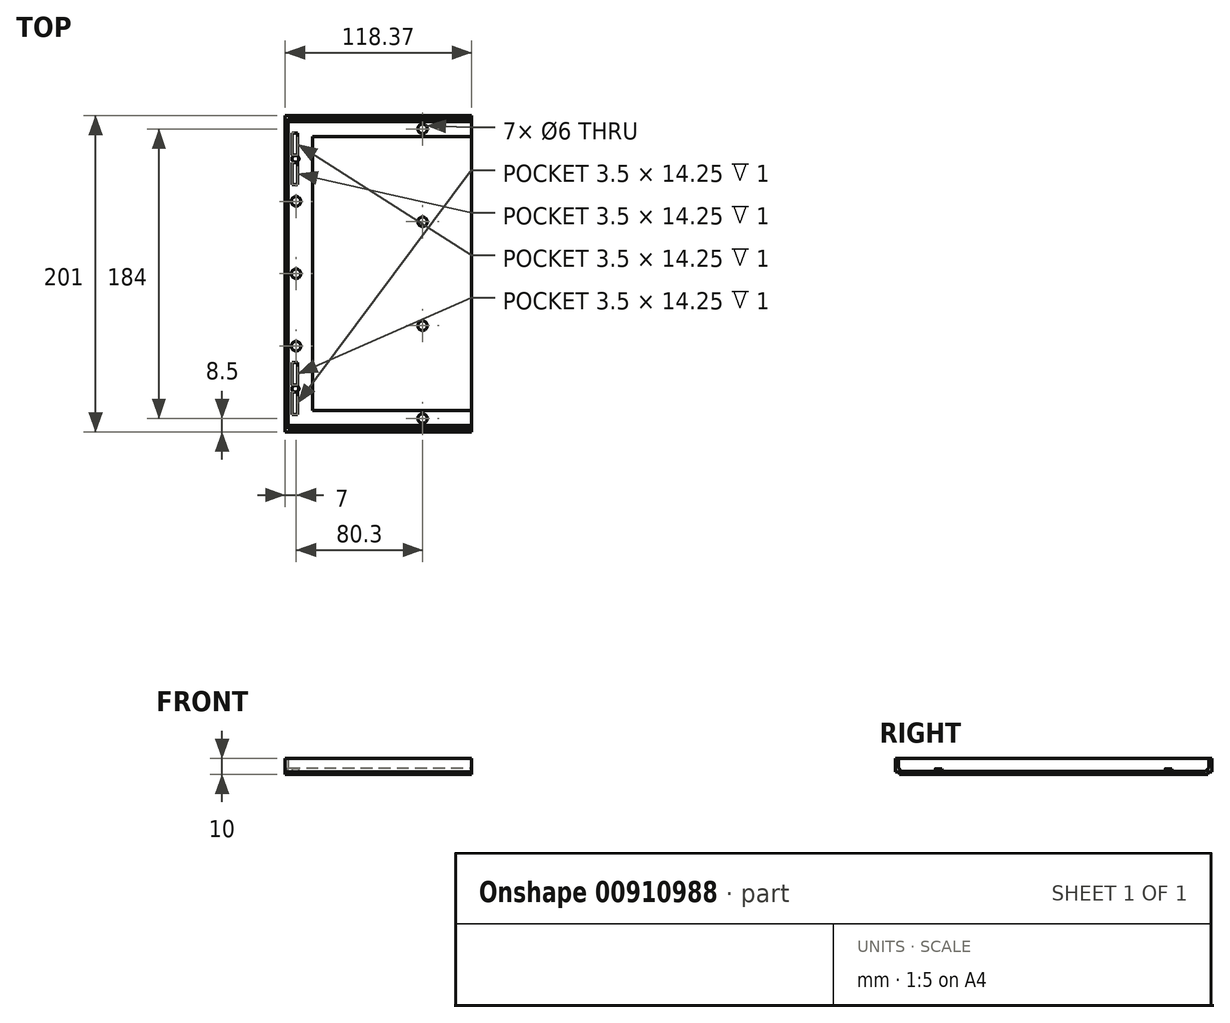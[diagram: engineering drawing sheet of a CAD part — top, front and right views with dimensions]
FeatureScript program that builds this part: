
annotation { "Feature Type Name" : "Feature", "Feature Type Description" : "" }
export const myFeature = defineFeature(function(context is Context, id is Id, definition is map)
    precondition{}
    {
        {
            var Q0;
            Q0=qCreatedBy(makeId("Top.planeOp"),FACE);
            var sketch = newSketch(context, id + "F0", { "sketchPlane" : qUnion([Q0])});
            skLineSegment(sketch, "E0.bottom", {"start": v(0, 0) * mm, "end": v(245, 0) * mm});
            skLineSegment(sketch, "E0.top", {"start": v(0, -201) * mm, "end": v(245, -201) * mm});
            skLineSegment(sketch, "E0.left", {"start": v(0, 0) * mm, "end": v(0, -201) * mm});
            skLineSegment(sketch, "E0.right", {"start": v(245, 0) * mm, "end": v(245, -201) * mm});
            skSolve(sketch);
        }
        {
            var Q0;
            Q0=qSketchRegion(id+"F0",true);
            extrude(context, id + "F1", {"entities" : qUnion([Q0]), "depth" : 8 * mm, "offsetDistance" : 25 * mm});
        }
        {
            var Q0;
            Q0=makeQuery(id+"F1.opExtrude","CAP_FACE",FACE,{"disambiguationData":[OSD([sQuery(id+"F0.wireOp",EDGE,"E0.bottom"),sQuery(id+"F0.wireOp",EDGE,"E0.top"),sQuery(id+"F0.wireOp",EDGE,"E0.left"),sQuery(id+"F0.wireOp",EDGE,"E0.right")])],"isStart":false});
            shell(context, id + "F2", {"entities" : qUnion([Q0]), "thickness" : 2 * mm});
        }
        {
            var Q0;
            Q0=makeQuery(id+"F2.opShell","OFFSET_FACE",FACE,{"disambiguationData":[OSD([sQuery(id+"F0.wireOp",EDGE,"E0.bottom"),sQuery(id+"F0.wireOp",EDGE,"E0.top"),sQuery(id+"F0.wireOp",EDGE,"E0.left"),sQuery(id+"F0.wireOp",EDGE,"E0.right")])]});
            var sketch = newSketch(context, id + "F3", { "sketchPlane" : qUnion([Q0])});
            skLineSegment(sketch, "E1.bottom", {"start": v(17.5, -13.5) * mm, "end": v(227.5, -13.5) * mm});
            skLineSegment(sketch, "E1.top", {"start": v(17.5, -187.5) * mm, "end": v(227.5, -187.5) * mm});
            skLineSegment(sketch, "E1.left", {"start": v(17.5, -13.5) * mm, "end": v(17.5, -187.5) * mm});
            skLineSegment(sketch, "E1.right", {"start": v(227.5, -13.5) * mm, "end": v(227.5, -187.5) * mm});
            skSolve(sketch);
        }
        {
            var Q0;
            Q0=qSketchRegion(id+"F3",true);
            extrude(context, id + "F4", {"entities" : qUnion([Q0]), "operationType" : NewBodyOperationType.REMOVE, "oppositeDirection" : true, "depth" : 1 * mm, "offsetDistance" : 25 * mm});
        }
        {
            var Q0;
            Q0=makeQuery(id+"F2.opShell","OFFSET_FACE",FACE,{"disambiguationData":[OSD([sQuery(id+"F0.wireOp",EDGE,"E0.bottom"),sQuery(id+"F0.wireOp",EDGE,"E0.top"),sQuery(id+"F0.wireOp",EDGE,"E0.left"),sQuery(id+"F0.wireOp",EDGE,"E0.right")])]});
            var sketch = newSketch(context, id + "F5", { "sketchPlane" : qUnion([Q0])});
            skLineSegment(sketch, "E2.bottom", {"start": v(4.5, -11) * mm, "end": v(8, -11) * mm});
            skLineSegment(sketch, "E2.top", {"start": v(4.5, -44) * mm, "end": v(8, -44) * mm});
            skLineSegment(sketch, "E2.left", {"start": v(4.5, -11) * mm, "end": v(4.5, -44) * mm});
            skLineSegment(sketch, "E2.right", {"start": v(8, -11) * mm, "end": v(8, -44) * mm});
            skLineSegment(sketch, "E3.bottom", {"start": v(4.5, -157) * mm, "end": v(8, -157) * mm});
            skLineSegment(sketch, "E3.top", {"start": v(4.5, -190) * mm, "end": v(8, -190) * mm});
            skLineSegment(sketch, "E3.left", {"start": v(4.5, -157) * mm, "end": v(4.5, -190) * mm});
            skLineSegment(sketch, "E3.right", {"start": v(8, -157) * mm, "end": v(8, -190) * mm});
            skLineSegment(sketch, "E4.bottom", {"start": v(237, -11) * mm, "end": v(240.5, -11) * mm});
            skLineSegment(sketch, "E4.top", {"start": v(237, -44) * mm, "end": v(240.5, -44) * mm});
            skLineSegment(sketch, "E4.left", {"start": v(237, -11) * mm, "end": v(237, -44) * mm});
            skLineSegment(sketch, "E4.right", {"start": v(240.5, -11) * mm, "end": v(240.5, -44) * mm});
            skLineSegment(sketch, "E5.bottom", {"start": v(237, -157) * mm, "end": v(240.5, -157) * mm});
            skLineSegment(sketch, "E5.top", {"start": v(237, -190) * mm, "end": v(240.5, -190) * mm});
            skLineSegment(sketch, "E5.left", {"start": v(237, -157) * mm, "end": v(237, -190) * mm});
            skLineSegment(sketch, "E5.right", {"start": v(240.5, -157) * mm, "end": v(240.5, -190) * mm});
            skSolve(sketch);
        }
        {
            var Q0;
            Q0=qSketchRegion(id+"F5",true);
            extrude(context, id + "F6", {"entities" : qUnion([Q0]), "operationType" : NewBodyOperationType.REMOVE, "oppositeDirection" : true, "depth" : 1 * mm, "offsetDistance" : 25 * mm});
        }
        {
            var Q0;
            Q0=makeQuery(id+"F2.opShell","OFFSET_FACE",FACE,{"disambiguationData":[OSD([sQuery(id+"F0.wireOp",EDGE,"E0.bottom"),sQuery(id+"F0.wireOp",EDGE,"E0.top"),sQuery(id+"F0.wireOp",EDGE,"E0.left"),sQuery(id+"F0.wireOp",EDGE,"E0.right")])]});
            var sketch = newSketch(context, id + "F7", { "sketchPlane" : qUnion([Q0])});
            skCircle(sketch, "E6", {"center": v(238, -7) * mm, "radius": 2.75 * mm});
            skCircle(sketch, "E7", {"center": v(7, -7) * mm, "radius": 2.75 * mm});
            skCircle(sketch, "E8", {"center": v(7, -194) * mm, "radius": 2.75 * mm});
            skCircle(sketch, "E9", {"center": v(238, -194) * mm, "radius": 2.75 * mm});
            skSolve(sketch);
        }
        {
            var Q0;
            Q0=makeQuery(id+"F2.opShell","OFFSET_FACE",FACE,{"disambiguationData":[OSD([sQuery(id+"F0.wireOp",EDGE,"E0.bottom"),sQuery(id+"F0.wireOp",EDGE,"E0.top"),sQuery(id+"F0.wireOp",EDGE,"E0.left"),sQuery(id+"F0.wireOp",EDGE,"E0.right")])]});
            var sketch = newSketch(context, id + "F8", { "sketchPlane" : qUnion([Q0])});
            skLineSegment(sketch, "E10", {"start": v(237, -175.75) * mm, "end": v(240.5, -175.75) * mm});
            skLineSegment(sketch, "E11", {"start": v(240.5, -175.75) * mm, "end": v(240.5, -171.25) * mm});
            skLineSegment(sketch, "E12", {"start": v(240.5, -171.25) * mm, "end": v(237, -171.25) * mm});
            skLineSegment(sketch, "E13", {"start": v(237, -175.75) * mm, "end": v(237, -171.25) * mm});
            skLineSegment(sketch, "E14.bottom", {"start": v(240.5, -25.25) * mm, "end": v(237, -25.25) * mm});
            skLineSegment(sketch, "E14.top", {"start": v(240.5, -29.75) * mm, "end": v(237, -29.75) * mm});
            skLineSegment(sketch, "E14.left", {"start": v(240.5, -25.25) * mm, "end": v(240.5, -29.75) * mm});
            skLineSegment(sketch, "E14.right", {"start": v(237, -25.25) * mm, "end": v(237, -29.75) * mm});
            skLineSegment(sketch, "E15.bottom", {"start": v(8, -25.25) * mm, "end": v(4.5, -25.25) * mm});
            skLineSegment(sketch, "E15.top", {"start": v(8, -29.75) * mm, "end": v(4.5, -29.75) * mm});
            skLineSegment(sketch, "E15.left", {"start": v(8, -25.25) * mm, "end": v(8, -29.75) * mm});
            skLineSegment(sketch, "E15.right", {"start": v(4.5, -25.25) * mm, "end": v(4.5, -29.75) * mm});
            skLineSegment(sketch, "E16.bottom", {"start": v(8, -175.75) * mm, "end": v(4.5, -175.75) * mm});
            skLineSegment(sketch, "E16.top", {"start": v(8, -171.25) * mm, "end": v(4.5, -171.25) * mm});
            skLineSegment(sketch, "E16.left", {"start": v(8, -175.75) * mm, "end": v(8, -171.25) * mm});
            skLineSegment(sketch, "E16.right", {"start": v(4.5, -175.75) * mm, "end": v(4.5, -171.25) * mm});
            skSolve(sketch);
        }
        {
            var Q0;
            Q0=qSketchRegion(id+"F8",true);
            extrude(context, id + "F9", {"entities" : qUnion([Q0]), "operationType" : NewBodyOperationType.ADD, "oppositeDirection" : true, "depth" : 1 * mm, "offsetDistance" : 25 * mm});
        }
        {
            var Q0;
            Q0=makeQuery(id+"F9.boolean.opBoolean","MERGE",FACE,{"derivedFrom":[makeQuery(id+"F2.opShell","OFFSET_FACE",FACE,{"disambiguationData":[OSD([sQuery(id+"F0.wireOp",EDGE,"E0.bottom"),sQuery(id+"F0.wireOp",EDGE,"E0.top"),sQuery(id+"F0.wireOp",EDGE,"E0.left"),sQuery(id+"F0.wireOp",EDGE,"E0.right")])]}),makeQuery(id+"F9.opExtrude","CAP_FACE",FACE,{"disambiguationData":[OSD([sQuery(id+"F8.wireOp",EDGE,"E10"),sQuery(id+"F8.wireOp",EDGE,"E11"),sQuery(id+"F8.wireOp",EDGE,"E12"),sQuery(id+"F8.wireOp",EDGE,"E13")])],"isStart":true}),makeQuery(id+"F9.opExtrude","CAP_FACE",FACE,{"disambiguationData":[OSD([sQuery(id+"F8.wireOp",EDGE,"E14.bottom"),sQuery(id+"F8.wireOp",EDGE,"E14.top"),sQuery(id+"F8.wireOp",EDGE,"E14.left"),sQuery(id+"F8.wireOp",EDGE,"E14.right")])],"isStart":true}),makeQuery(id+"F9.opExtrude","CAP_FACE",FACE,{"disambiguationData":[OSD([sQuery(id+"F8.wireOp",EDGE,"E15.bottom"),sQuery(id+"F8.wireOp",EDGE,"E15.top"),sQuery(id+"F8.wireOp",EDGE,"E15.left"),sQuery(id+"F8.wireOp",EDGE,"E15.right")])],"isStart":true}),makeQuery(id+"F9.opExtrude","CAP_FACE",FACE,{"disambiguationData":[OSD([sQuery(id+"F8.wireOp",EDGE,"E16.bottom"),sQuery(id+"F8.wireOp",EDGE,"E16.top"),sQuery(id+"F8.wireOp",EDGE,"E16.left"),sQuery(id+"F8.wireOp",EDGE,"E16.right")])],"isStart":true})]});
            var sketch = newSketch(context, id + "F10", { "sketchPlane" : qUnion([Q0])});
            skCircle(sketch, "E17", {"center": v(238.5, -27.5) * mm, "radius": 2.25 * mm});
            skCircle(sketch, "E18", {"center": v(6.5, -27.5) * mm, "radius": 2.25 * mm});
            skCircle(sketch, "E19", {"center": v(6.5, -173.5) * mm, "radius": 2.25 * mm});
            skCircle(sketch, "E20", {"center": v(238.5, -173.5) * mm, "radius": 2.25 * mm});
            skCircle(sketch, "E21", {"center": v(122.5, -8.5) * mm, "radius": 2.25 * mm});
            skSolve(sketch);
        }
        {
            var Q0;
            Q0=qSketchRegion(id+"F10",true);
            extrude(context, id + "F11", {"entities" : qUnion([Q0]), "operationType" : NewBodyOperationType.ADD, "depth" : 1.5 * mm, "offsetDistance" : 25 * mm});
        }
        {
            var Q0;
            Q0=makeQuery(id+"F11.opExtrude","CAP_EDGE",EDGE,{"disambiguationData":[OSD([sQuery(id+"F10.wireOp",EDGE,"E20")])],"isStart":false});
            var Q1;
            Q1=makeQuery(id+"F11.opExtrude","CAP_EDGE",EDGE,{"disambiguationData":[OSD([sQuery(id+"F10.wireOp",EDGE,"E19")])],"isStart":false});
            var Q2;
            Q2=makeQuery(id+"F11.opExtrude","CAP_EDGE",EDGE,{"disambiguationData":[OSD([sQuery(id+"F10.wireOp",EDGE,"E17")])],"isStart":false});
            var Q3;
            Q3=makeQuery(id+"F11.opExtrude","CAP_EDGE",EDGE,{"disambiguationData":[OSD([sQuery(id+"F10.wireOp",EDGE,"E18")])],"isStart":false});
            var Q4;
            Q4=makeQuery(id+"F11.opExtrude","CAP_EDGE",EDGE,{"disambiguationData":[OSD([sQuery(id+"F10.wireOp",EDGE,"E21")])],"isStart":false});
            chamfer(context, id + "F12", {"entities" : qUnion([Q0, Q1, Q2, Q3, Q4]), "chamferType" : ChamferType.OFFSET_ANGLE, "width" : .15 * mm, "oppositeDirection" : false, "angle" : 84.25 * degree, "tangentPropagation" : true});
        }
        {
            var Q0;
            Q0=makeQuery(id+"F9.boolean.opBoolean","MERGE",FACE,{"derivedFrom":[makeQuery(id+"F2.opShell","OFFSET_FACE",FACE,{"disambiguationData":[OSD([sQuery(id+"F0.wireOp",EDGE,"E0.bottom"),sQuery(id+"F0.wireOp",EDGE,"E0.top"),sQuery(id+"F0.wireOp",EDGE,"E0.left"),sQuery(id+"F0.wireOp",EDGE,"E0.right")])]}),makeQuery(id+"F9.opExtrude","CAP_FACE",FACE,{"disambiguationData":[OSD([sQuery(id+"F8.wireOp",EDGE,"E10"),sQuery(id+"F8.wireOp",EDGE,"E11"),sQuery(id+"F8.wireOp",EDGE,"E12"),sQuery(id+"F8.wireOp",EDGE,"E13")])],"isStart":true}),makeQuery(id+"F9.opExtrude","CAP_FACE",FACE,{"disambiguationData":[OSD([sQuery(id+"F8.wireOp",EDGE,"E14.bottom"),sQuery(id+"F8.wireOp",EDGE,"E14.top"),sQuery(id+"F8.wireOp",EDGE,"E14.left"),sQuery(id+"F8.wireOp",EDGE,"E14.right")])],"isStart":true}),makeQuery(id+"F9.opExtrude","CAP_FACE",FACE,{"disambiguationData":[OSD([sQuery(id+"F8.wireOp",EDGE,"E15.bottom"),sQuery(id+"F8.wireOp",EDGE,"E15.top"),sQuery(id+"F8.wireOp",EDGE,"E15.left"),sQuery(id+"F8.wireOp",EDGE,"E15.right")])],"isStart":true}),makeQuery(id+"F9.opExtrude","CAP_FACE",FACE,{"disambiguationData":[OSD([sQuery(id+"F8.wireOp",EDGE,"E16.bottom"),sQuery(id+"F8.wireOp",EDGE,"E16.top"),sQuery(id+"F8.wireOp",EDGE,"E16.left"),sQuery(id+"F8.wireOp",EDGE,"E16.right")])],"isStart":true})]});
            var sketch = newSketch(context, id + "F13", { "sketchPlane" : qUnion([Q0])});
            skCircle(sketch, "E22", {"center": v(7, -54.5) * mm, "radius": 3 * mm});
            skCircle(sketch, "E23", {"center": v(7, -100.5) * mm, "radius": 3 * mm});
            skCircle(sketch, "E24", {"center": v(7, -146.5) * mm, "radius": 3 * mm});
            skCircle(sketch, "E25.MirrorC", {"center": v(238, -54.5) * mm, "radius": 3 * mm});
            skCircle(sketch, "E26.MirrorC", {"center": v(238, -100.5) * mm, "radius": 3 * mm});
            skCircle(sketch, "E27.MirrorC", {"center": v(238, -146.5) * mm, "radius": 3 * mm});
            skCircle(sketch, "E28", {"center": v(87.3, -8.5) * mm, "radius": 3 * mm});
            skCircle(sketch, "E29", {"center": v(87.3, -67.5) * mm, "radius": 3 * mm});
            skPoint(sketch, "E30.0", {"position": v(122.5, -12.5) * mm});
            skPoint(sketch, "E31.MirrorP", {"position": v(122.5, -364.5) * mm});
            skPoint(sketch, "E32.MirrorP", {"position": v(122.5, -188.5) * mm});
            skCircle(sketch, "E33.MirrorC", {"center": v(157.7, -8.5) * mm, "radius": 3 * mm});
            skCircle(sketch, "E34.MirrorC", {"center": v(157.7, -67.5) * mm, "radius": 3 * mm});
            skCircle(sketch, "E35.MirrorC", {"center": v(157.7, -133.5) * mm, "radius": 3 * mm});
            skCircle(sketch, "E36.MirrorC", {"center": v(157.7, -192.5) * mm, "radius": 3 * mm});
            skCircle(sketch, "E37.MirrorC", {"center": v(87.3, -192.5) * mm, "radius": 3 * mm});
            skCircle(sketch, "E38.MirrorC", {"center": v(87.3, -133.5) * mm, "radius": 3 * mm});
            skSolve(sketch);
        }
        {
            var Q0;
            Q0=qSketchRegion(id+"F13",true);
            extrude(context, id + "F14", {"entities" : qUnion([Q0]), "operationType" : NewBodyOperationType.REMOVE, "endBound" : BoundingType.THROUGH_ALL, "oppositeDirection" : true, "depth" : 25 * mm, "offsetDistance" : 25 * mm});
        }
        {
            var Q0;
            Q0=makeQuery(id+"F1.opExtrude","SWEPT_FACE",FACE,{"disambiguationData":[OSD([sQuery(id+"F0.wireOp",EDGE,"E0.left")])]});
            var sketch = newSketch(context, id + "F15", { "sketchPlane" : qUnion([Q0])});
            skLineSegment(sketch, "E39.bottom", {"start": v(2.5, 0) * mm, "end": v(0, 0) * mm});
            skLineSegment(sketch, "E39.top", {"start": v(2.5, 1.5) * mm, "end": v(0, 1.5) * mm});
            skLineSegment(sketch, "E39.left", {"start": v(2.5, 0) * mm, "end": v(2.5, 1.5) * mm});
            skLineSegment(sketch, "E39.right", {"start": v(0, 0) * mm, "end": v(0, 1.5) * mm});
            skPoint(sketch, "E40.oppositeSnap0", {"position": v(1.25, 1.5) * mm});
            skLineSegment(sketch, "E40.bottom", {"start": v(198.5, 0) * mm, "end": v(201, 0) * mm});
            skLineSegment(sketch, "E40.top", {"start": v(198.5, 1.5) * mm, "end": v(201, 1.5) * mm});
            skLineSegment(sketch, "E40.left", {"start": v(198.5, 0) * mm, "end": v(198.5, 1.5) * mm});
            skLineSegment(sketch, "E40.right", {"start": v(201, 0) * mm, "end": v(201, 1.5) * mm});
            skSolve(sketch);
        }
        {
            var Q0;
            Q0=qSketchRegion(id+"F15",true);
            extrude(context, id + "F16", {"entities" : qUnion([Q0]), "operationType" : NewBodyOperationType.REMOVE, "endBound" : BoundingType.THROUGH_ALL, "oppositeDirection" : true, "depth" : 25 * mm, "offsetDistance" : 25 * mm});
        }
        {
            var Q0;
            {var subQ0=sQuery(id+"F0.wireOp",EDGE,"E0.bottom");Q0=makeQuery(id+"F2.opShell","OFFSET_EDGE",EDGE,{"disambiguationData":[OSD([subQ0]),TDD([makeQuery(id+"F1.opExtrude","CAP_EDGE",EDGE,{"disambiguationData":[OSD([subQ0])],"isStart":true})])]});}
            var Q1;
            {var subQ0=sQuery(id+"F0.wireOp",EDGE,"E0.top");Q1=makeQuery(id+"F2.opShell","OFFSET_EDGE",EDGE,{"disambiguationData":[OSD([subQ0]),TDD([makeQuery(id+"F1.opExtrude","CAP_EDGE",EDGE,{"disambiguationData":[OSD([subQ0])],"isStart":true})])]});}
            chamfer(context, id + "F17", {"entities" : qUnion([Q0, Q1]), "width" : 2 * mm, "tangentPropagation" : true});
        }
        {
            var Q0;
            Q0=makeQuery(id+"F1.opExtrude","CAP_FACE",FACE,{"disambiguationData":[OSD([sQuery(id+"F0.wireOp",EDGE,"E0.bottom"),sQuery(id+"F0.wireOp",EDGE,"E0.top"),sQuery(id+"F0.wireOp",EDGE,"E0.left"),sQuery(id+"F0.wireOp",EDGE,"E0.right")])],"isStart":false});
            extrude(context, id + "F18", {"entities" : qUnion([Q0]), "operationType" : NewBodyOperationType.ADD, "depth" : 2 * mm, "offsetDistance" : 25 * mm});
        }
        {
            var Q0;
            Q0=makeQuery(id+"F1.opExtrude","CAP_FACE",FACE,{"disambiguationData":[OSD([sQuery(id+"F0.wireOp",EDGE,"E0.bottom"),sQuery(id+"F0.wireOp",EDGE,"E0.top"),sQuery(id+"F0.wireOp",EDGE,"E0.left"),sQuery(id+"F0.wireOp",EDGE,"E0.right")])],"isStart":true});
            var sketch = newSketch(context, id + "F19", { "sketchPlane" : qUnion([Q0])});
            skLineSegment(sketch, "E41.bottom", {"start": v(305.12, -20.79) * mm, "end": v(118.37, -20.79) * mm});
            skLineSegment(sketch, "E41.top", {"start": v(305.12, 228.81) * mm, "end": v(118.37, 228.81) * mm});
            skLineSegment(sketch, "E41.left", {"start": v(118.37, -20.79) * mm, "end": v(118.37, 228.81) * mm});
            skLineSegment(sketch, "E41.right", {"start": v(305.12, -20.79) * mm, "end": v(305.12, 228.81) * mm});
            skSolve(sketch);
        }
        {
            var Q0;
            Q0 = qSketchRegion(id + "F19", true);
            extrude(context, id + "F20", {"entities" : qUnion([Q0]), "operationType" : NewBodyOperationType.REMOVE, "endBound" : BoundingType.THROUGH_ALL, "oppositeDirection" : true, "depth" : 25 * mm, "offsetDistance" : 25 * mm});
        }
    });
